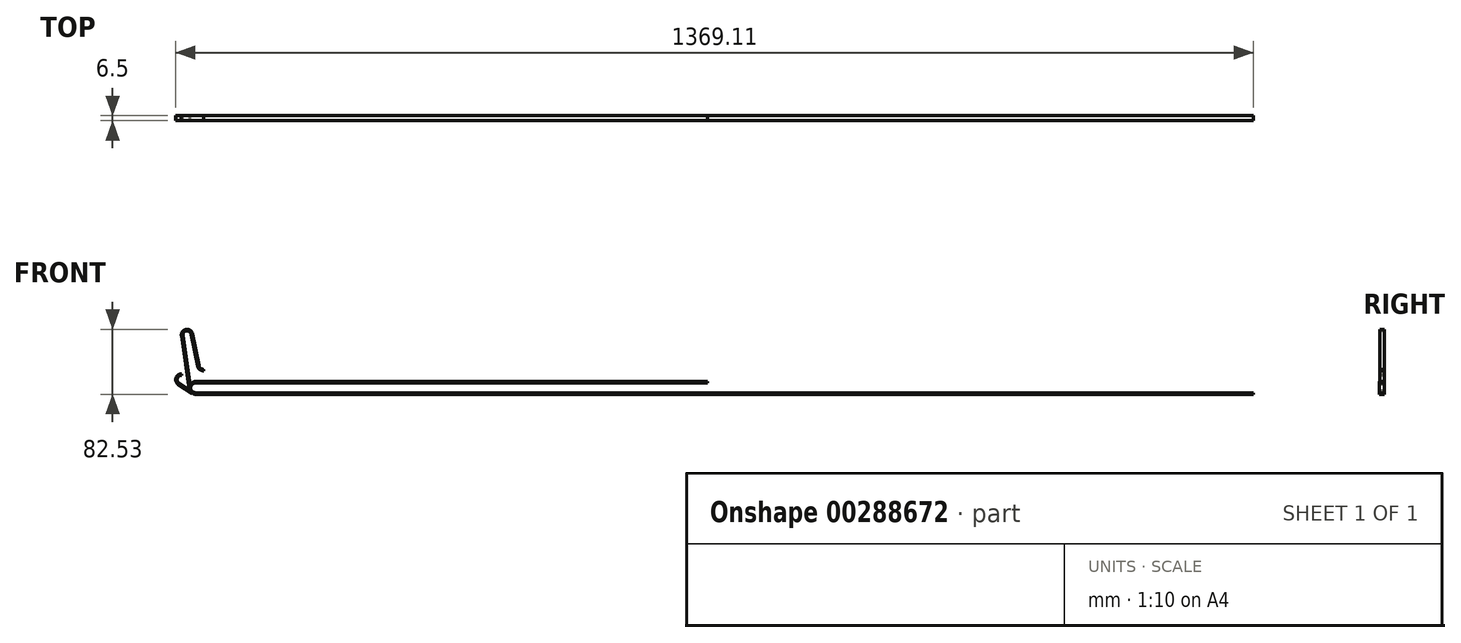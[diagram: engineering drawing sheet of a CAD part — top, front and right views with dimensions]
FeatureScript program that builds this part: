
annotation { "Feature Type Name" : "Feature", "Feature Type Description" : "" }
export const myFeature = defineFeature(function(context is Context, id is Id, definition is map)
    precondition{}
    {
        {
            var Q0;
            Q0=qCreatedBy(makeId("Front.planeOp"),FACE);
            var sketch = newSketch(context, id + "F0", { "sketchPlane" : qUnion([Q0])});
            skLineSegment(sketch, "E0", {"start": v(-141.03, 0) * mm, "end": v(192.33, 0) * mm, "construction": true});
            skLineSegment(sketch, "E1.0", {"start": v(-141.03, 6.1) * mm, "end": v(1127.96, 6.1) * mm, "construction": true});
            skLineSegment(sketch, "E2.0", {"start": v(-141.03, 12.2) * mm, "end": v(192.33, 12.2) * mm, "construction": true});
            skLineSegment(sketch, "E3.0", {"start": v(-141.03, 29.68) * mm, "end": v(192.33, 29.68) * mm, "construction": true});
            skLineSegment(sketch, "E4.0", {"start": v(-141.03, 35.78) * mm, "end": v(192.33, 35.78) * mm, "construction": true});
            skLineSegment(sketch, "E5.0", {"start": v(-141.03, 41.88) * mm, "end": v(192.33, 41.88) * mm, "construction": true});
            skLineSegment(sketch, "E6.0", {"start": v(-141.03, 67.93) * mm, "end": v(192.33, 67.93) * mm, "construction": true});
            skLineSegment(sketch, "E7.0", {"start": v(-141.03, 73.23) * mm, "end": v(192.33, 73.23) * mm, "construction": true});
            skLineSegment(sketch, "E8.0", {"start": v(-141.03, 78.53) * mm, "end": v(192.33, 78.53) * mm, "construction": true});
            skLineSegment(sketch, "E9", {"start": v(-103.22, 95.96) * mm, "end": v(-103.22, -21.71) * mm, "construction": true});
            skLineSegment(sketch, "E10.0", {"start": v(-97.92, 95.96) * mm, "end": v(-97.92, -21.71) * mm, "construction": true});
            skLineSegment(sketch, "E11.0", {"start": v(-92.62, 95.96) * mm, "end": v(-92.62, -21.71) * mm, "construction": true});
            skLineSegment(sketch, "E12.0", {"start": v(-93.22, 95.96) * mm, "end": v(-93.22, -21.71) * mm, "construction": true});
            skLineSegment(sketch, "E13.0", {"start": v(-87.12, 95.96) * mm, "end": v(-87.12, -21.71) * mm, "construction": true});
            skLineSegment(sketch, "E14.0", {"start": v(-81.02, 95.96) * mm, "end": v(-81.02, -21.71) * mm, "construction": true});
            skCircle(sketch, "E15", {"center": v(-87.12, 6.1) * mm, "radius": 6.1 * mm});
            skCircle(sketch, "E16", {"center": v(-97.92, 73.23) * mm, "radius": 5.3 * mm});
            skLineSegment(sketch, "E17.0", {"start": v(-82.97, 95.96) * mm, "end": v(-82.97, -21.71) * mm, "construction": true});
            skLineSegment(sketch, "E18.0", {"start": v(-76.87, 95.96) * mm, "end": v(-76.87, -21.71) * mm, "construction": true});
            skLineSegment(sketch, "E19.0", {"start": v(-70.77, 95.96) * mm, "end": v(-70.77, -21.71) * mm, "construction": true});
            skCircle(sketch, "E20", {"center": v(-76.87, 35.78) * mm, "radius": 6.1 * mm});
            skArc(sketch, "E21.0", {"start": v(-81.8, 0) * mm, "mid": v(-81.84, 12.23) * mm, "end": v(-93.94, 10.47) * mm});
            skArc(sketch, "E22.0", {"start": v(-71.55, 29.68) * mm, "mid": v(-71.73, 42.04) * mm, "end": v(-83.9, 39.83) * mm});
            skArc(sketch, "E23.0", {"start": v(-103.22, 68.2) * mm, "mid": v(-103.09, 68.07) * mm, "end": v(-102.94, 67.93) * mm, "construction": true});
            skLineSegment(sketch, "E24", {"start": v(-95.14, 4.9) * mm, "end": v(-105.15, 72.15) * mm});
            skLineSegment(sketch, "E25", {"start": v(-84.82, 34.21) * mm, "end": v(-92.72, 74.25) * mm});
            skPoint(sketch, "E25.endSnap0", {"position": v(-92.62, 37.12) * mm});
            skArc(sketch, "E26.trimOffspring", {"start": v(-103.77, 68.85) * mm, "mid": v(-103.38, 68.37) * mm, "end": v(-102.94, 67.93) * mm, "construction": true});
            skLineSegment(sketch, "E27", {"start": v(-82.86, 34.6) * mm, "end": v(-90.76, 74.64) * mm});
            skLineSegment(sketch, "E28", {"start": v(-103.17, 72.45) * mm, "end": v(-93.16, 5.2) * mm});
            skArc(sketch, "E29.trimOffspring", {"start": v(-102.43, 67.48) * mm, "mid": v(-96.68, 66.03) * mm, "end": v(-91.75, 69.33) * mm});
            skLineSegment(sketch, "E30", {"start": v(-76.87, 29.68) * mm, "end": v(117.86, 29.68) * mm});
            skLineSegment(sketch, "E31", {"start": v(117.86, 29.68) * mm, "end": v(117.86, -7.37) * mm});
            skLineSegment(sketch, "E32", {"start": v(-87.12, 0) * mm, "end": v(117.86, 0) * mm});
            skLineSegment(sketch, "E33", {"start": v(-76.87, 27.68) * mm, "end": v(117.86, 27.68) * mm});
            skLineSegment(sketch, "E34", {"start": v(-87.12, -2) * mm, "end": v(117.86, -2) * mm});
            skArc(sketch, "E35.trimOffspring", {"start": v(-84.82, 34.21) * mm, "mid": v(-82.02, 29.53) * mm, "end": v(-76.87, 27.68) * mm});
            skArc(sketch, "E36.trimOffspring", {"start": v(-95.14, 4.9) * mm, "mid": v(-92.41, -0.03) * mm, "end": v(-87.12, -2) * mm});
            skArc(sketch, "E37.trimOffspring", {"start": v(-90.76, 74.64) * mm, "mid": v(-99.17, 80.42) * mm, "end": v(-105.15, 72.15) * mm});
            skLineSegment(sketch, "E38", {"start": v(-76.87, 29.68) * mm, "end": v(-76.87, 27.68) * mm});
            skCircle(sketch, "E39", {"center": v(-87.12, 6.1) * mm, "radius": 8.1 * mm});
            skLineSegment(sketch, "E40", {"start": v(-87.12, 12.2) * mm, "end": v(-87.12, 14.2) * mm});
            skLineSegment(sketch, "E41.0", {"start": v(1033.74, 95.96) * mm, "end": v(1033.74, -21.71) * mm, "construction": true});
            skCircle(sketch, "E42", {"center": v(1033.74, 6.1) * mm, "radius": 6.1 * mm});
            skLineSegment(sketch, "E43.0", {"start": v(-141.03, 16.6) * mm, "end": v(1127.96, 16.6) * mm, "construction": true});
            skLineSegment(sketch, "E44.0", {"start": v(-105.12, 95.96) * mm, "end": v(-105.12, -21.71) * mm, "construction": true});
            skCircle(sketch, "E45", {"center": v(-105.12, 16.6) * mm, "radius": 5.3 * mm});
            skCircle(sketch, "E46", {"center": v(-105.12, 16.6) * mm, "radius": 7.3 * mm});
            skLineSegment(sketch, "E47", {"start": v(-91.47, -0.73) * mm, "end": v(-109.04, 10.44) * mm});
            skLineSegment(sketch, "E48", {"start": v(-107.97, 12.13) * mm, "end": v(-90.4, 0.95) * mm});
            skLineSegment(sketch, "E49", {"start": v(-105.05, 23.9) * mm, "end": v(1033.74, 12.2) * mm, "construction": true});
            skLineSegment(sketch, "E50", {"start": v(-105.05, 23.9) * mm, "end": v(-105.12, 21.9) * mm});
            skSolve(sketch);
        }
        {
            var Q0;
            Q0=makeQuery(id+"F0.imprint","IMPRINT",FACE,{"disambiguationData":[TD([[makeQuery(id+"F0.imprint","IMPRINT",EDGE,{"derivedFrom":sQuery(id+"F0.wireOp",EDGE,"E24")}),-1.0]])]});
            var Q1;
            {var subQ1=sQuery(id+"F0.wireOp",EDGE,"E15");var subQ6=sQuery(id+"F0.wireOp",EDGE,"E28");var subQ8=makeQuery(id+"F0.imprint","INTERSECT",VERTEX,{"derivedFrom":[subQ1,subQ6]});Q1=makeQuery(id+"F0.imprint","IMPRINT",FACE,{"disambiguationData":[TD([[makeQuery(id+"F0.imprint","IMPRINT",EDGE,{"disambiguationData":[TD([[subQ8,-1.0]])],"derivedFrom":subQ1}),-1.0]])]});}
            var Q2;
            {var subQ3=sQuery(id+"F0.wireOp",EDGE,"E34");Q2=makeQuery(id+"F0.imprint","IMPRINT",FACE,{"disambiguationData":[TD([[makeQuery(id+"F0.imprint","IMPRINT",EDGE,{"derivedFrom":subQ3}),1.0]])]});}
            var Q3;
            {var subQ3=sQuery(id+"F0.wireOp",EDGE,"E32");var subQ4=sQuery(id+"F0.wireOp",EDGE,"E15");var subQ5=makeQuery(id+"F0.imprint","INTERSECT",VERTEX,{"derivedFrom":[subQ4,subQ3]});Q3=makeQuery(id+"F0.imprint","IMPRINT",FACE,{"disambiguationData":[TD([[makeQuery(id+"F0.imprint","IMPRINT",EDGE,{"disambiguationData":[TD([[subQ5,1.0]])],"derivedFrom":subQ4}),-1.0]])]});}
            extrude(context, id + "F1", {"entities" : qUnion([Q0, Q1, Q2, Q3]), "depth" : 6 * mm});
        }
        {
            var Q0;
            {var subQ3=sQuery(id+"F0.wireOp",EDGE,"E32");var subQ4=sQuery(id+"F0.wireOp",EDGE,"E15");var subQ5=makeQuery(id+"F0.imprint","INTERSECT",VERTEX,{"derivedFrom":[subQ4,subQ3]});Q0=makeQuery(id+"F0.imprint","IMPRINT",FACE,{"disambiguationData":[TD([[makeQuery(id+"F0.imprint","IMPRINT",EDGE,{"disambiguationData":[TD([[subQ5,1.0]])],"derivedFrom":subQ4}),-1.0]])]});}
            var Q1;
            {var subQ3=sQuery(id+"F0.wireOp",EDGE,"E40");Q1=makeQuery(id+"F0.imprint","IMPRINT",FACE,{"disambiguationData":[TD([[makeQuery(id+"F0.imprint","IMPRINT",EDGE,{"derivedFrom":subQ3}),1.0]])]});}
            var Q2;
            {var subQ4=sQuery(id+"F0.wireOp",EDGE,"E28");var subQ6=sQuery(id+"F0.wireOp",EDGE,"E15");var subQ7=makeQuery(id+"F0.imprint","INTERSECT",VERTEX,{"derivedFrom":[subQ6,subQ4]});Q2=makeQuery(id+"F0.imprint","IMPRINT",FACE,{"disambiguationData":[TD([[makeQuery(id+"F0.imprint","IMPRINT",EDGE,{"disambiguationData":[TD([[subQ7,-1.0]])],"derivedFrom":subQ6}),-1.0]])]});}
            var Q3;
            {var subQ3=sQuery(id+"F0.wireOp",EDGE,"E34");Q3=makeQuery(id+"F0.imprint","IMPRINT",FACE,{"disambiguationData":[TD([[makeQuery(id+"F0.imprint","IMPRINT",EDGE,{"derivedFrom":subQ3}),1.0]])]});}
            extrude(context, id + "F2", {"entities" : qUnion([Q0, Q1, Q2, Q3]), "depth" : 6 * mm});
        }
        {
            var Q0;
            Q0=makeQuery(id+"F1.opExtrude","SWEPT_FACE",FACE,{"disambiguationData":[OSD([sQuery(id+"F0.wireOp",EDGE,"E31")])]});
            extrude(context, id + "F3", {"entities" : qUnion([Q0]), "depth" : 1124.75 * mm});
        }
        {
            var Q0;
            Q0=makeQuery(id+"F1.opExtrude","SWEPT_FACE",FACE,{"disambiguationData":[OSD([sQuery(id+"F0.wireOp",EDGE,"E31")])]});
            extrude(context, id + "F4", {"entities" : qUnion([Q0]), "depth" : 900 * mm});
        }
        {
            var Q0;
            {var subQ6=sQuery(id+"F0.wireOp",EDGE,"E50");Q0=makeQuery(id+"F0.imprint","IMPRINT",FACE,{"disambiguationData":[TD([[makeQuery(id+"F0.imprint","IMPRINT",EDGE,{"derivedFrom":subQ6}),-1.0]])]});}
            var Q1;
            {var subQ0=sQuery(id+"F0.wireOp",EDGE,"E47");Q1=makeQuery(id+"F0.imprint","IMPRINT",FACE,{"disambiguationData":[TD([[makeQuery(id+"F0.imprint","IMPRINT",EDGE,{"derivedFrom":subQ0}),-1.0]])]});}
            var Q2;
            {var subQ3=sQuery(id+"F0.wireOp",EDGE,"E32");var subQ4=sQuery(id+"F0.wireOp",EDGE,"E15");var subQ5=makeQuery(id+"F0.imprint","INTERSECT",VERTEX,{"derivedFrom":[subQ4,subQ3]});Q2=makeQuery(id+"F0.imprint","IMPRINT",FACE,{"disambiguationData":[TD([[makeQuery(id+"F0.imprint","IMPRINT",EDGE,{"disambiguationData":[TD([[subQ5,1.0]])],"derivedFrom":subQ4}),-1.0]])]});}
            var Q3;
            {var subQ3=sQuery(id+"F0.wireOp",EDGE,"E34");Q3=makeQuery(id+"F0.imprint","IMPRINT",FACE,{"disambiguationData":[TD([[makeQuery(id+"F0.imprint","IMPRINT",EDGE,{"derivedFrom":subQ3}),1.0]])]});}
            extrude(context, id + "F5", {"entities" : qUnion([Q0, Q1, Q2, Q3]), "depth" : 6 * mm});
        }
        {
            var Q0;
            Q0=makeQuery(id+"F5.opExtrude","SWEPT_FACE",FACE,{"disambiguationData":[OSD([sQuery(id+"F0.wireOp",EDGE,"E31")])]});
            extrude(context, id + "F6", {"entities" : qUnion([Q0]), "depth" : 1138.83 * mm});
        }
        {
            var Q0;
            {var subQ3=sQuery(id+"F0.wireOp",EDGE,"E40");Q0=makeQuery(id+"F0.imprint","IMPRINT",FACE,{"disambiguationData":[TD([[makeQuery(id+"F0.imprint","IMPRINT",EDGE,{"derivedFrom":subQ3}),1.0]])]});}
            var Q1;
            {var subQ4=sQuery(id+"F0.wireOp",EDGE,"E28");var subQ6=sQuery(id+"F0.wireOp",EDGE,"E15");var subQ7=makeQuery(id+"F0.imprint","INTERSECT",VERTEX,{"derivedFrom":[subQ6,subQ4]});Q1=makeQuery(id+"F0.imprint","IMPRINT",FACE,{"disambiguationData":[TD([[makeQuery(id+"F0.imprint","IMPRINT",EDGE,{"disambiguationData":[TD([[subQ7,-1.0]])],"derivedFrom":subQ6}),-1.0]])]});}
            var Q2;
            {var subQ3=sQuery(id+"F0.wireOp",EDGE,"E32");var subQ4=sQuery(id+"F0.wireOp",EDGE,"E15");var subQ5=makeQuery(id+"F0.imprint","INTERSECT",VERTEX,{"derivedFrom":[subQ4,subQ3]});Q2=makeQuery(id+"F0.imprint","IMPRINT",FACE,{"disambiguationData":[TD([[makeQuery(id+"F0.imprint","IMPRINT",EDGE,{"disambiguationData":[TD([[subQ5,1.0]])],"derivedFrom":subQ4}),-1.0]])]});}
            var Q3;
            {var subQ3=sQuery(id+"F0.wireOp",EDGE,"E34");Q3=makeQuery(id+"F0.imprint","IMPRINT",FACE,{"disambiguationData":[TD([[makeQuery(id+"F0.imprint","IMPRINT",EDGE,{"derivedFrom":subQ3}),1.0]])]});}
            extrude(context, id + "F7", {"entities" : qUnion([Q0, Q1, Q2, Q3]), "depth" : 6.5 * mm});
        }
        {
            var Q0;
            Q0=makeQuery(id+"F7.opExtrude","SWEPT_FACE",FACE,{"disambiguationData":[OSD([sQuery(id+"F0.wireOp",EDGE,"E40")])]});
            extrude(context, id + "F8", {"entities" : qUnion([Q0]), "operationType" : NewBodyOperationType.ADD, "depth" : 650 * mm});
        }
        {
            var Q0;
            Q0=makeQuery(id+"F7.opExtrude","SWEPT_FACE",FACE,{"disambiguationData":[OSD([sQuery(id+"F0.wireOp",EDGE,"E31")])]});
            var Q1;
            Q1=makeQuery(id+"F8.opExtrude","CAP_FACE",FACE,{"disambiguationData":[OSD([sQuery(id+"F0.wireOp",EDGE,"E40")])],"isStart":false});
            extrude(context, id + "F9", {"entities" : qUnion([Q0]), "operationType" : NewBodyOperationType.ADD, "endBound" : BoundingType.UP_TO_SURFACE, "endBoundEntityFace" : qUnion([Q1]), "depth" : 25 * mm});
        }
    });
